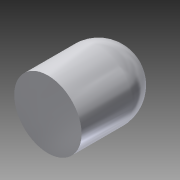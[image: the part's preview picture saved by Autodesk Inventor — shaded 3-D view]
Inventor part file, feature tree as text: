
AUTODESK INVENTOR PART (.ipt)
format: ipt  version: 2015 (Build 190159000, 159)  size: 95,744 bytes
history: native  units: mm
features: extrude x1, fillet x1, sketch x1
ambient origin geometry x8: Origin, YZ Plane, XZ Plane, XY Plane, X Axis, Y Axis, Z Axis, Center Point
bodies: Solid1 (feature_tree)
feature tree (3):
  extrude  "Extrusion1"  Depth=10.0mm TaperAngle=0.0deg
  fillet  "Fillet1"  Radius=4.0mm
  sketch  "Sketch1"  dims[d0=8.0mm d1=10.0mm d2=0.0mm d3=4.0mm]
